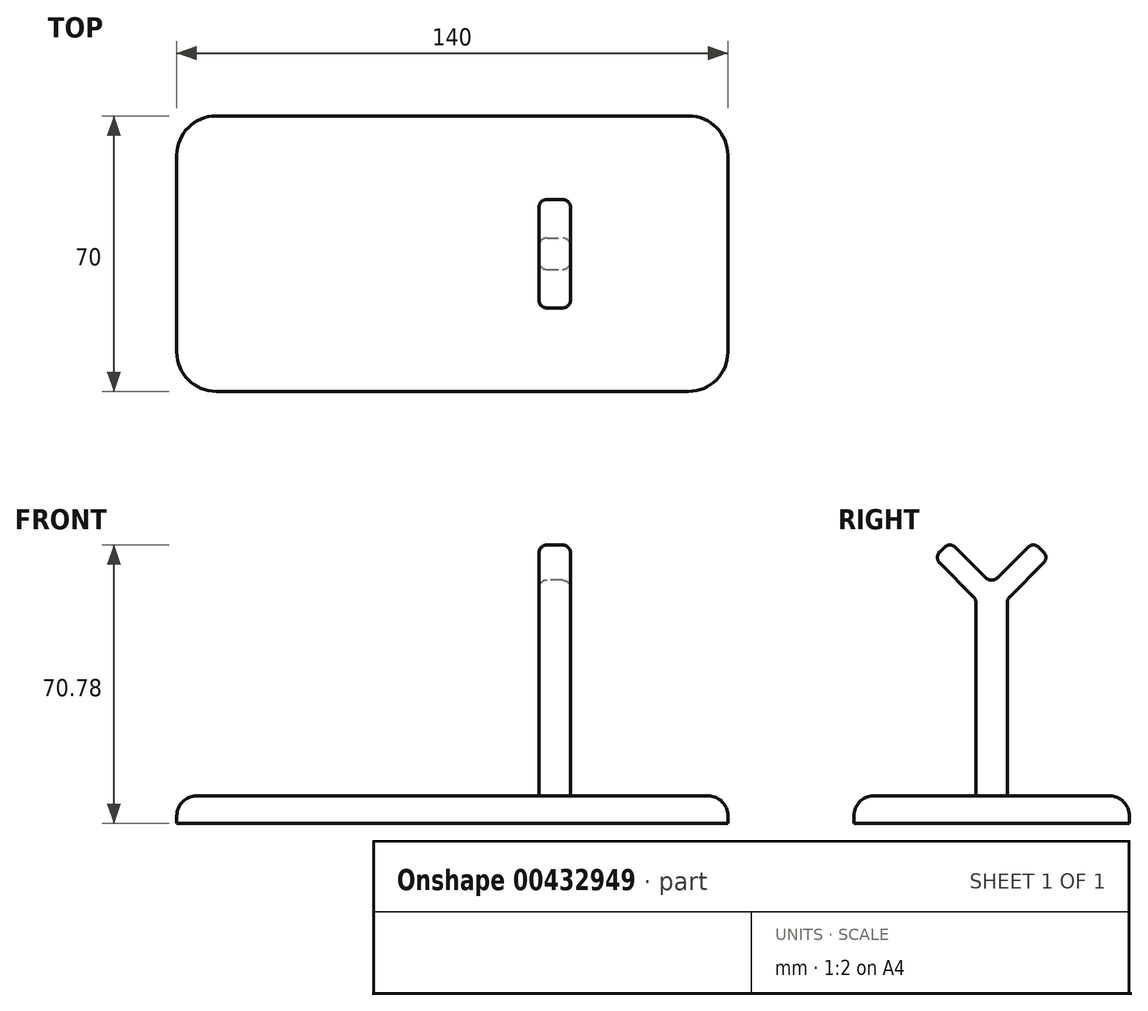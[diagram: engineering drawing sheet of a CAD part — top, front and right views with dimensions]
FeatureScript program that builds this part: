
annotation { "Feature Type Name" : "Feature", "Feature Type Description" : "" }
export const myFeature = defineFeature(function(context is Context, id is Id, definition is map)
    precondition{}
    {
        {
            var Q0;
            Q0=qCreatedBy(makeId("Top.planeOp"),FACE);
            var sketch = newSketch(context, id + "F0", { "sketchPlane" : qUnion([Q0])});
            skLineSegment(sketch, "E0.bottom", {"start": v(70, 35) * mm, "end": v(-70, 35) * mm});
            skLineSegment(sketch, "E0.top", {"start": v(70, -35) * mm, "end": v(-70, -35) * mm});
            skLineSegment(sketch, "E0.left", {"start": v(70, 35) * mm, "end": v(70, -35) * mm});
            skLineSegment(sketch, "E0.right", {"start": v(-70, 35) * mm, "end": v(-70, -35) * mm});
            skPoint(sketch, "E0.middle", {"position": v(0, 0) * mm});
            skSolve(sketch);
        }
        {
            var Q0;
            Q0=makeQuery(id+"F0.imprint","IMPRINT",FACE,{"disambiguationData":[TD([[makeQuery(id+"F0.imprint","IMPRINT",EDGE,{"derivedFrom":sQuery(id+"F0.wireOp",EDGE,"E0.bottom")}),1.0]])]});
            extrude(context, id + "F1", {"entities" : qUnion([Q0]), "depth" : 7 * mm});
        }
        {
            var Q0;
            Q0=makeQuery(id+"F1.opExtrude","CAP_FACE",FACE,{"disambiguationData":[OSD([sQuery(id+"F0.wireOp",EDGE,"E0.bottom"),sQuery(id+"F0.wireOp",EDGE,"E0.top"),sQuery(id+"F0.wireOp",EDGE,"E0.left"),sQuery(id+"F0.wireOp",EDGE,"E0.right")])],"isStart":false});
            var sketch = newSketch(context, id + "F2", { "sketchPlane" : qUnion([Q0])});
            skLineSegment(sketch, "E1.bottom", {"start": v(22, 4) * mm, "end": v(30, 4) * mm});
            skLineSegment(sketch, "E1.top", {"start": v(22, -4) * mm, "end": v(30, -4) * mm});
            skLineSegment(sketch, "E1.left", {"start": v(22, 4) * mm, "end": v(22, -4) * mm});
            skLineSegment(sketch, "E1.right", {"start": v(30, 4) * mm, "end": v(30, -4) * mm});
            skPoint(sketch, "E1.middle", {"position": v(26, 0) * mm});
            skSolve(sketch);
        }
        {
            var Q0;
            Q0=makeQuery(id+"F2.imprint","IMPRINT",FACE,{"disambiguationData":[TD([[makeQuery(id+"F2.imprint","IMPRINT",EDGE,{"derivedFrom":sQuery(id+"F2.wireOp",EDGE,"E1.bottom")}),-1.0]])]});
            extrude(context, id + "F3", {"entities" : qUnion([Q0]), "operationType" : NewBodyOperationType.ADD, "depth" : 50 * mm});
        }
        {
            var Q0;
            Q0=makeQuery(id+"F3.opExtrude","SWEPT_FACE",FACE,{"disambiguationData":[OSD([sQuery(id+"F2.wireOp",EDGE,"E1.right")])]});
            var sketch = newSketch(context, id + "F4", { "sketchPlane" : qUnion([Q0])});
            skLineSegment(sketch, "E2", {"start": v(-4, 57) * mm, "end": v(-14.6, 67.6) * mm});
            skLineSegment(sketch, "E3", {"start": v(-14.6, 67.6) * mm, "end": v(-10.6, 71.6) * mm});
            skLineSegment(sketch, "E4", {"start": v(-10.6, 71.6) * mm, "end": v(0, 61) * mm});
            skLineSegment(sketch, "E5", {"start": v(0, 61) * mm, "end": v(10.6, 71.6) * mm});
            skLineSegment(sketch, "E6", {"start": v(10.6, 71.6) * mm, "end": v(14.6, 67.6) * mm});
            skLineSegment(sketch, "E7", {"start": v(14.6, 67.6) * mm, "end": v(4, 57) * mm});
            skLineSegment(sketch, "E8", {"start": v(-4, 57) * mm, "end": v(4, 57) * mm});
            skSolve(sketch);
        }
        {
            var Q0;
            Q0 = qSketchRegion(id + "F4", true);
            extrude(context, id + "F5", {"entities" : qUnion([Q0]), "oppositeDirection" : true, "depth" : 8 * mm});
        }
        {
            var Q0;
            Q0=makeQuery(id+"F1.opExtrude","SWEPT_EDGE",EDGE,{"disambiguationData":[OSD([sQuery(id+"F0.wireOp",EDGE,"E0.bottom"),sQuery(id+"F0.wireOp",EDGE,"E0.right")])]});
            var Q1;
            Q1=makeQuery(id+"F1.opExtrude","SWEPT_EDGE",EDGE,{"disambiguationData":[OSD([sQuery(id+"F0.wireOp",EDGE,"E0.top"),sQuery(id+"F0.wireOp",EDGE,"E0.right")])]});
            var Q2;
            Q2=makeQuery(id+"F1.opExtrude","SWEPT_EDGE",EDGE,{"disambiguationData":[OSD([sQuery(id+"F0.wireOp",EDGE,"E0.bottom"),sQuery(id+"F0.wireOp",EDGE,"E0.left")])]});
            var Q3;
            Q3=makeQuery(id+"F1.opExtrude","SWEPT_EDGE",EDGE,{"disambiguationData":[OSD([sQuery(id+"F0.wireOp",EDGE,"E0.top"),sQuery(id+"F0.wireOp",EDGE,"E0.left")])]});
            fillet(context, id + "F6", {"entities" : qUnion([Q0, Q1, Q2, Q3]), "radius" : 10 * mm, "tangentPropagation" : true, "allowEdgeOverflow" : false});
        }
        {
            var Q0;
            Q0=makeQuery(id+"F1.opExtrude","CAP_EDGE",EDGE,{"disambiguationData":[OSD([sQuery(id+"F0.wireOp",EDGE,"E0.top")])],"isStart":false});
            var Q1;
            Q1=makeQuery(id+"F1.opExtrude","CAP_EDGE",EDGE,{"disambiguationData":[OSD([sQuery(id+"F0.wireOp",EDGE,"E0.left")])],"isStart":false});
            var Q2;
            Q2=makeQuery(id+"F1.opExtrude","CAP_EDGE",EDGE,{"disambiguationData":[OSD([sQuery(id+"F0.wireOp",EDGE,"E0.bottom")])],"isStart":false});
            var Q3;
            Q3=makeQuery(id+"F1.opExtrude","CAP_EDGE",EDGE,{"disambiguationData":[OSD([sQuery(id+"F0.wireOp",EDGE,"E0.right")])],"isStart":false});
            fillet(context, id + "F7", {"entities" : qUnion([Q0, Q1, Q2, Q3]), "radius" : 5 * mm, "tangentPropagation" : true, "allowEdgeOverflow" : false});
        }
        {
            var Q0;
            Q0=makeQuery(id+"F1.opExtrude","SWEPT_BODY",BODY,{"disambiguationData":[OSD([sQuery(id+"F0.wireOp",EDGE,"E0.bottom"),sQuery(id+"F0.wireOp",EDGE,"E0.top"),sQuery(id+"F0.wireOp",EDGE,"E0.left"),sQuery(id+"F0.wireOp",EDGE,"E0.right")])]});
            var Q1;
            Q1=makeQuery(id+"F5.opExtrude","SWEPT_BODY",BODY,{"disambiguationData":[OSD([sQuery(id+"F4.wireOp",EDGE,"E2"),sQuery(id+"F4.wireOp",EDGE,"E3"),sQuery(id+"F4.wireOp",EDGE,"E4"),sQuery(id+"F4.wireOp",EDGE,"E5"),sQuery(id+"F4.wireOp",EDGE,"E6"),sQuery(id+"F4.wireOp",EDGE,"E7"),sQuery(id+"F4.wireOp",EDGE,"E8")])]});
            booleanBodies(context, id + "F8", {"operationType" : BooleanOperationType.UNION, "tools" : qUnion([Q0, Q1])});
        }
        {
            var Q0;
            Q0=makeQuery(id+"F5.opExtrude","CAP_EDGE",EDGE,{"disambiguationData":[OSD([sQuery(id+"F4.wireOp",EDGE,"E7")])],"isStart":true});
            var Q1;
            Q1=makeQuery(id+"F3.opExtrude","SWEPT_EDGE",EDGE,{"disambiguationData":[OSD([sQuery(id+"F2.wireOp",EDGE,"E1.bottom"),sQuery(id+"F2.wireOp",EDGE,"E1.right")])]});
            var Q2;
            Q2=makeQuery(id+"F5.opExtrude","CAP_EDGE",EDGE,{"disambiguationData":[OSD([sQuery(id+"F4.wireOp",EDGE,"E5")])],"isStart":true});
            var Q3;
            Q3=makeQuery(id+"F5.opExtrude","CAP_EDGE",EDGE,{"disambiguationData":[OSD([sQuery(id+"F4.wireOp",EDGE,"E4")])],"isStart":true});
            var Q4;
            Q4=makeQuery(id+"F5.opExtrude","CAP_EDGE",EDGE,{"disambiguationData":[OSD([sQuery(id+"F4.wireOp",EDGE,"E2")])],"isStart":true});
            var Q5;
            Q5=makeQuery(id+"F3.opExtrude","SWEPT_EDGE",EDGE,{"disambiguationData":[OSD([sQuery(id+"F2.wireOp",EDGE,"E1.top"),sQuery(id+"F2.wireOp",EDGE,"E1.right")])]});
            var Q6;
            Q6=makeQuery(id+"F5.opExtrude","SWEPT_EDGE",EDGE,{"disambiguationData":[OSD([sQuery(id+"F4.wireOp",EDGE,"E5"),sQuery(id+"F4.wireOp",EDGE,"E6")])]});
            var Q7;
            Q7=makeQuery(id+"F5.opExtrude","SWEPT_EDGE",EDGE,{"disambiguationData":[OSD([sQuery(id+"F4.wireOp",EDGE,"E3"),sQuery(id+"F4.wireOp",EDGE,"E4")])]});
            var Q8;
            Q8=makeQuery(id+"F5.opExtrude","SWEPT_EDGE",EDGE,{"disambiguationData":[OSD([sQuery(id+"F4.wireOp",EDGE,"E4"),sQuery(id+"F4.wireOp",EDGE,"E5")])]});
            var Q9;
            Q9=makeQuery(id+"F5.opExtrude","SWEPT_EDGE",EDGE,{"disambiguationData":[OSD([sQuery(id+"F4.wireOp",EDGE,"E6"),sQuery(id+"F4.wireOp",EDGE,"E7")])]});
            var Q10;
            Q10=makeQuery(id+"F5.opExtrude","CAP_EDGE",EDGE,{"disambiguationData":[OSD([sQuery(id+"F4.wireOp",EDGE,"E3")])],"isStart":true});
            var Q11;
            Q11=makeQuery(id+"F5.opExtrude","CAP_EDGE",EDGE,{"disambiguationData":[OSD([sQuery(id+"F4.wireOp",EDGE,"E6")])],"isStart":true});
            var Q12;
            Q12=makeQuery(id+"F5.opExtrude","CAP_EDGE",EDGE,{"disambiguationData":[OSD([sQuery(id+"F4.wireOp",EDGE,"E6")])],"isStart":false});
            var Q13;
            Q13=makeQuery(id+"F5.opExtrude","CAP_EDGE",EDGE,{"disambiguationData":[OSD([sQuery(id+"F4.wireOp",EDGE,"E4")])],"isStart":false});
            var Q14;
            {var subQ0=sQuery(id+"F2.wireOp",EDGE,"E1.top");Q14=makeQuery(id+"F8.opBoolean","MERGE",EDGE,{"derivedFrom":[makeQuery(id+"F3.opExtrude","CAP_EDGE",EDGE,{"disambiguationData":[OSD([subQ0])],"isStart":false}),makeQuery(id+"F5.opExtrude","SWEPT_EDGE",EDGE,{"disambiguationData":[OSD([subQ0,sQuery(id+"F2.wireOp",EDGE,"E1.right"),sQuery(id+"F4.wireOp",EDGE,"E2"),sQuery(id+"F4.wireOp",EDGE,"E8")])]})]});}
            var Q15;
            Q15=makeQuery(id+"F3.opExtrude","SWEPT_EDGE",EDGE,{"disambiguationData":[OSD([sQuery(id+"F2.wireOp",EDGE,"E1.top"),sQuery(id+"F2.wireOp",EDGE,"E1.left")])]});
            var Q16;
            Q16=makeQuery(id+"F5.opExtrude","CAP_EDGE",EDGE,{"disambiguationData":[OSD([sQuery(id+"F4.wireOp",EDGE,"E2")])],"isStart":false});
            var Q17;
            Q17=makeQuery(id+"F5.opExtrude","SWEPT_EDGE",EDGE,{"disambiguationData":[OSD([sQuery(id+"F4.wireOp",EDGE,"E2"),sQuery(id+"F4.wireOp",EDGE,"E3")])]});
            var Q18;
            Q18=makeQuery(id+"F5.opExtrude","CAP_EDGE",EDGE,{"disambiguationData":[OSD([sQuery(id+"F4.wireOp",EDGE,"E3")])],"isStart":false});
            var Q19;
            Q19=makeQuery(id+"F5.opExtrude","CAP_EDGE",EDGE,{"disambiguationData":[OSD([sQuery(id+"F4.wireOp",EDGE,"E5")])],"isStart":false});
            var Q20;
            Q20=makeQuery(id+"F5.opExtrude","CAP_EDGE",EDGE,{"disambiguationData":[OSD([sQuery(id+"F4.wireOp",EDGE,"E7")])],"isStart":false});
            var Q21;
            Q21=makeQuery(id+"F3.opExtrude","SWEPT_EDGE",EDGE,{"disambiguationData":[OSD([sQuery(id+"F2.wireOp",EDGE,"E1.bottom"),sQuery(id+"F2.wireOp",EDGE,"E1.left")])]});
            var Q22;
            {var subQ0=sQuery(id+"F2.wireOp",EDGE,"E1.bottom");Q22=makeQuery(id+"F8.opBoolean","MERGE",EDGE,{"derivedFrom":[makeQuery(id+"F3.opExtrude","CAP_EDGE",EDGE,{"disambiguationData":[OSD([subQ0])],"isStart":false}),makeQuery(id+"F5.opExtrude","SWEPT_EDGE",EDGE,{"disambiguationData":[OSD([subQ0,sQuery(id+"F2.wireOp",EDGE,"E1.right"),sQuery(id+"F4.wireOp",EDGE,"E7"),sQuery(id+"F4.wireOp",EDGE,"E8")])]})]});}
            var Q23;
            Q23=makeQuery(id+"F3.opExtrude","CAP_EDGE",EDGE,{"disambiguationData":[OSD([sQuery(id+"F2.wireOp",EDGE,"E1.left")])],"isStart":true});
            var Q24;
            Q24=makeQuery(id+"F3.opExtrude","CAP_EDGE",EDGE,{"disambiguationData":[OSD([sQuery(id+"F2.wireOp",EDGE,"E1.bottom")])],"isStart":true});
            var Q25;
            Q25=makeQuery(id+"F3.opExtrude","CAP_EDGE",EDGE,{"disambiguationData":[OSD([sQuery(id+"F2.wireOp",EDGE,"E1.right")])],"isStart":true});
            var Q26;
            Q26=makeQuery(id+"F3.opExtrude","CAP_EDGE",EDGE,{"disambiguationData":[OSD([sQuery(id+"F2.wireOp",EDGE,"E1.top")])],"isStart":true});
            fillet(context, id + "F9", {"entities" : qUnion([Q0, Q1, Q2, Q3, Q4, Q5, Q6, Q7, Q8, Q9, Q10, Q11, Q12, Q13, Q14, Q15, Q16, Q17, Q18, Q19, Q20, Q21, Q22, Q23, Q24, Q25, Q26]), "radius" : 2 * mm, "tangentPropagation" : true, "allowEdgeOverflow" : false});
        }
    });
